# Revit family: DC_Rheem_PLM_CPI3_WallMounted
name_source: partatom
category: Generic Models
revit_build: Autodesk Revit 2018 (Build: 20170223_1515(x64)
units: mm (PartAtom-declared; Revit-internal decimal feet)

## family parameters
Can host rebar = No
Cut with Voids When Loaded = No
Host = Face
Part Type = Normal
Room Calculation Point = No
Round Connector Dimension = Use Radius
Shared = No

## types (2) — shared parameters
ColdWaterRadius_ANZRS = 20 mm  [stored 0.0656168 ft]
GasRadius_ANZRS = 20 mm  [stored 0.0656168 ft]
HotWaterRadius_ANZRS = 20 mm  [stored 0.0656168 ft]
HotWaterReturnRadius_ANZRS = 13 mm
Manufacturer = Rheem
Material_ANZRS = Rheem - Antique White
PRVRadius_ANZRS = 13 mm
Stand Width = 995 mm  [stored 3.26444 ft]
Type Comments = 41L/min @ 50°C rise  - Separate secondary recirculation pump not required. Optional dual pump and controller available, quote part no. 299659.
URL = http://www.rheem.com.au
zero-valued in all types: Default Elevation

## per-type parameters (varying)
| type | Description |
| CPI03N0 | Commpak - Gas Continuous Flow- Indoor- 615 MJ/h Natural gas wall mount frame - single pump - recirculation and dead leg 60°C + |
| CPI03P0 | Commpak - Gas Continuous Flow- Indoor - 615 MJ/h Propane gas wall mount frame - single pump - recirculation and dead leg 60°C + |

note: column(s) folded — value = type name in every type: Model

note: [stored X ft] marks values corroborated as IEEE doubles in the binary element streams (Revit-internal decimal feet)

## geometry (parser evidence)
native form markers: Blend x4, Sweep x16
no freeform markers — native parametric forms only
